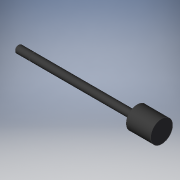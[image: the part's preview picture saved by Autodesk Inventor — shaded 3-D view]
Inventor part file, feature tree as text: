
AUTODESK INVENTOR PART (.ipt)
format: ipt  version: 2019 (Build 230136000, 136)  size: 162,304 bytes
history: native  units: in
note: dims shown in document units (in); Inventor stores cm internally (conversion verified against a paired STEP export)
features: other x70, revolve x3, sketch x3
ambient origin geometry x8: Origin, YZ Plane, XZ Plane, XY Plane, X Axis, Y Axis, Z Axis, Center Point
bodies: Solid1 (feature_tree)
feature tree (76):
  revolve  "Revolution1"  Angle=360.0deg
  revolve  "Revolution2"  [1 undecoded]
  revolve  "Revolution3"  [1 undecoded]
  other  "dia1_XY"
  other  "dia1_YZ"
  other  "dia1_ZX"
  other  "dia1_X"
  other  "dia1_Y"
  other  "dia1_Z"
  other  "dia1_Center"
  other  "dia12_XY"
  other  "dia12_YZ"
  other  "dia12_ZX"
  other  "dia12_X"
  other  "dia12_Y"
  other  "dia12_Z"
  other  "dia12_Center"
  other  "dia2_XY"
  other  "dia2_YZ"
  other  "dia2_ZX"
  other  "dia2_X"
  other  "dia2_Y"
  other  "dia2_Z"
  other  "dia2_Center"
  other  "dia22_XY"
  other  "dia22_YZ"
  other  "dia22_ZX"
  other  "dia22_X"
  other  "dia22_Y"
  other  "dia22_Z"
  other  "dia22_Center"
  other  "rl1_XY"
  other  "rl1_YZ"
  other  "rl1_ZX"
  other  "rl1_X"
  other  "rl1_Y"
  other  "rl1_Z"
  other  "rl1_Center"
  other  "rl2_XY"
  other  "rl2_YZ"
  other  "rl2_ZX"
  other  "rl2_X"
  other  "rl2_Y"
  other  "rl2_Z"
  other  "rl2_Center"
  other  "rod_cp_XY"
  other  "rod_cp_YZ"
  other  "rod_cp_ZX"
  other  "rod_cp_X"
  other  "rod_cp_Y"
  other  "rod_cp_Z"
  other  "rod_cp_Center"
  other  "thd1_XY"
  other  "thd1_YZ"
  other  "thd1_ZX"
  other  "thd1_X"
  other  "thd1_Y"
  other  "thd1_Z"
  other  "thd1_Center"
  other  "thd2_XY"
  other  "thd2_YZ"
  other  "thd2_ZX"
  other  "thd2_X"
  other  "thd2_Y"
  other  "thd2_Z"
  other  "thd2_Center"
  other  "to_rod_clevis_XY"
  other  "to_rod_clevis_YZ"
  other  "to_rod_clevis_ZX"
  other  "to_rod_clevis_X"
  other  "to_rod_clevis_Y"
  other  "to_rod_clevis_Z"
  other  "to_rod_clevis_Center"
  sketch  "Sketch_1"  dims[d0=360.0deg d1=360.0deg]
  sketch  "Sketch_3"  dims[d2=360.0deg]
  sketch  "Sketch_30"  dims[d3=0.0in d4=0.0in d5=0.0in d6=0.0in d7=0.0in]
note: 2 required parameter values undecoded (feature->parameter linkage not recoverable at this tier; creation-order binding heuristic only, values carry confidence <= 0.55)
